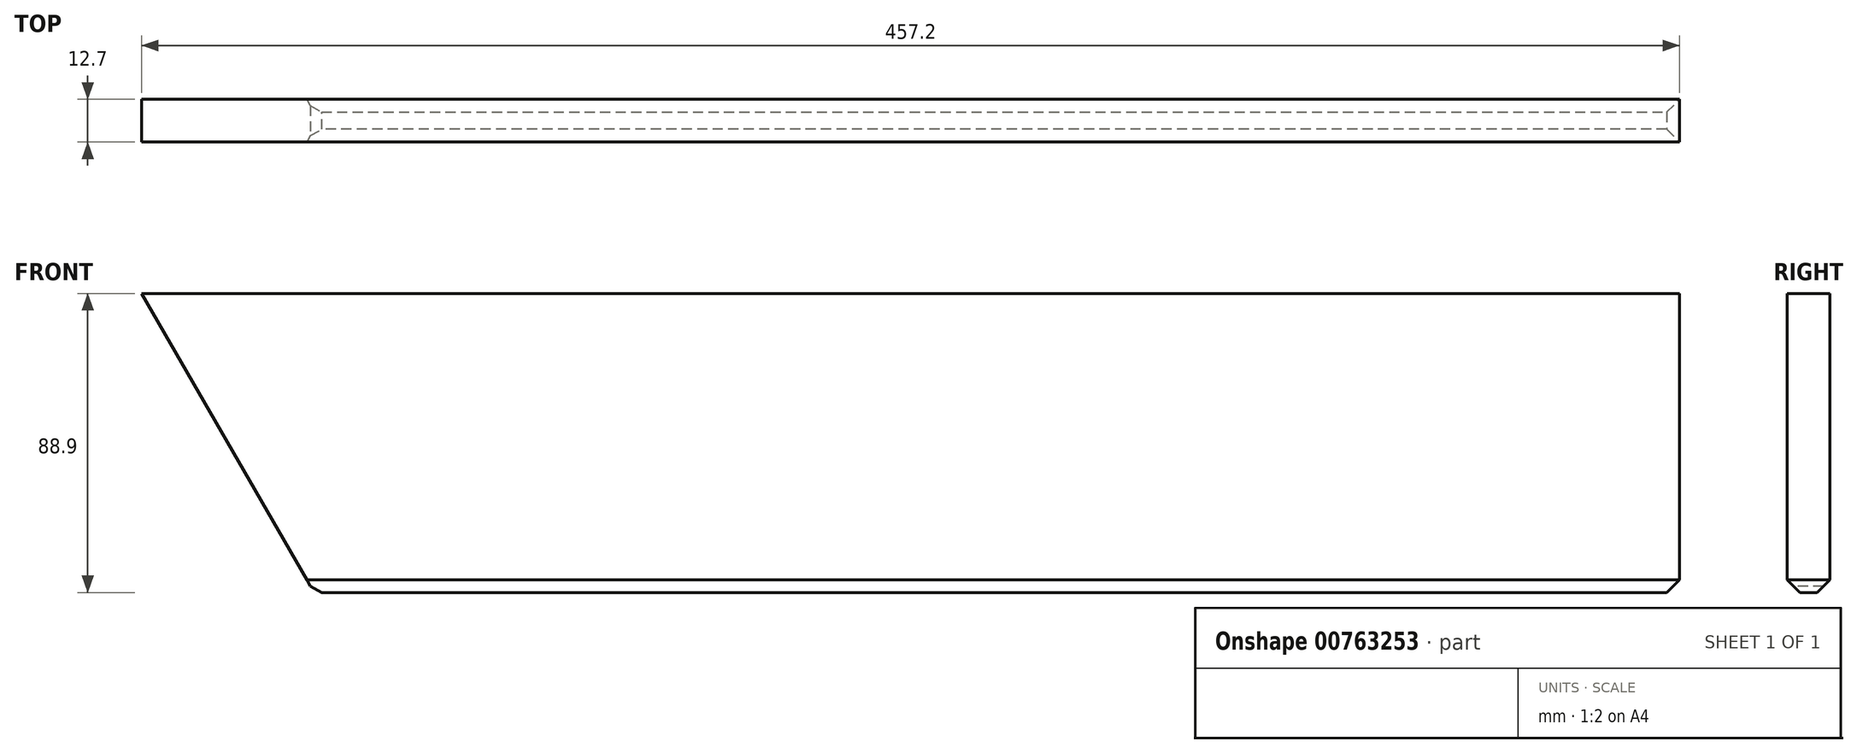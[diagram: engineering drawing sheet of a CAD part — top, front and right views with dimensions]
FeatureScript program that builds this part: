
annotation { "Feature Type Name" : "Feature", "Feature Type Description" : "" }
export const myFeature = defineFeature(function(context is Context, id is Id, definition is map)
    precondition{}
    {
        {
            var Q0;
            Q0=qCreatedBy(makeId("Front.planeOp"),FACE);
            var sketch = newSketch(context, id + "F0", { "sketchPlane" : qUnion([Q0])});
            skLineSegment(sketch, "E0.bottom", {"start": v(-228.6, 44.45) * mm, "end": v(228.6, 44.45) * mm});
            skLineSegment(sketch, "E0.top", {"start": v(-228.6, -44.45) * mm, "end": v(228.6, -44.45) * mm});
            skLineSegment(sketch, "E0.left", {"start": v(-228.6, 44.45) * mm, "end": v(-228.6, -44.45) * mm});
            skLineSegment(sketch, "E0.right", {"start": v(228.6, 44.45) * mm, "end": v(228.6, -44.45) * mm});
            skPoint(sketch, "E0.middle", {"position": v(0, 0) * mm});
            skSolve(sketch);
        }
        {
            var Q0;
            Q0 = qSketchRegion(id + "F0", true);
            extrude(context, id + "F1", {"entities" : qUnion([Q0]), "depth" : 12.7 * mm, "offsetDistance" : 25.4 * mm});
        }
        {
            var Q0;
            Q0=makeQuery(id+"F1.opExtrude","CAP_FACE",FACE,{"disambiguationData":[OSD([sQuery(id+"F0.wireOp",EDGE,"E0.bottom"),sQuery(id+"F0.wireOp",EDGE,"E0.top"),sQuery(id+"F0.wireOp",EDGE,"E0.left"),sQuery(id+"F0.wireOp",EDGE,"E0.right")])],"isStart":false});
            var sketch = newSketch(context, id + "F2", { "sketchPlane" : qUnion([Q0])});
            skLineSegment(sketch, "E1", {"start": v(-228.6, 44.45) * mm, "end": v(-177.27, -44.45) * mm});
            skLineSegment(sketch, "E2", {"start": v(-177.27, -44.45) * mm, "end": v(228.6, -44.45) * mm});
            skLineSegment(sketch, "E3", {"start": v(228.6, -44.45) * mm, "end": v(228.6, 44.45) * mm});
            skLineSegment(sketch, "E4", {"start": v(228.6, 44.45) * mm, "end": v(-228.6, 44.45) * mm});
            skSolve(sketch);
        }
        {
            var Q0;
            {var subQ0=sQuery(id+"F2.wireOp",EDGE,"E1");Q0=makeQuery(id+"F2.imprint","IMPRINT",FACE,{"disambiguationData":[TD([[makeQuery(id+"F2.imprint","IMPRINT",EDGE,{"derivedFrom":subQ0}),-1.0]])]});}
            extrude(context, id + "F3", {"entities" : qUnion([Q0]), "operationType" : NewBodyOperationType.REMOVE, "endBound" : BoundingType.THROUGH_ALL, "oppositeDirection" : true, "depth" : 25.4 * mm, "offsetDistance" : 25.4 * mm});
        }
        {
            var Q0;
            Q0=makeQuery(id+"F1.opExtrude","SWEPT_FACE",FACE,{"disambiguationData":[OSD([sQuery(id+"F0.wireOp",EDGE,"E0.top")])]});
            var Q1;
            Q1=makeQuery(id+"F3.boolean.opBoolean","COPY",FACE,{"derivedFrom":makeQuery(id+"F3.opExtrude","SWEPT_FACE",FACE,{"disambiguationData":[OSD([sQuery(id+"F2.wireOp",EDGE,"yO3eYtxi-ThZj-5d2g-wQ6I-LDxqYH7FaOcl")])]})});
            chamfer(context, id + "F4", {"entities" : qUnion([Q0, Q1]), "width" : 3.8 * mm});
        }
    });
